# Revit family: 1342-35-CHLI
name_source: partatom
category: Plumbing Fixtures
revit_build: Autodesk Revit 2014 (Build: 20130308_1515(x64)
units: mm (PartAtom-declared; Revit-internal decimal feet)

## types (1)
- 1342-35-CHLI
    Body = Iron, Cast
    CW Connection = Yes
    Description = Bathroom Drain With Round Three Outlets Grid Square For Insert
    Documentation = http://www.helvex.com.mx
    Drain = Forged Brass
    Elevation Range = 2.2" - 2.7"
    Features = Drain For Marmol or Ceramic Insert, Integrated Cesspool, Double Drain Plate, 0.23" (6 mm) to Dislodge Perimeter, Hydraulic Seal, 10 mm Insert Thickness, Maximum
    Insert Holder = Forged Brass
    Installation Thread = 2" - 11 ½ NPSM
    Manufacturer = Helvex
    Max. Water Flow = 8.8 gal/min
    Maximum Height = 9"
    Minimum Height = 8"
    Model = 1342-35-CHLI
    Plate Diameter = 8"
    Type Comments = Drains
    URL = http://www.helvex.com.mx
    Vent Connection = Yes

## geometry (parser evidence)
native form markers: Sweep x1
no freeform markers — native parametric forms only
